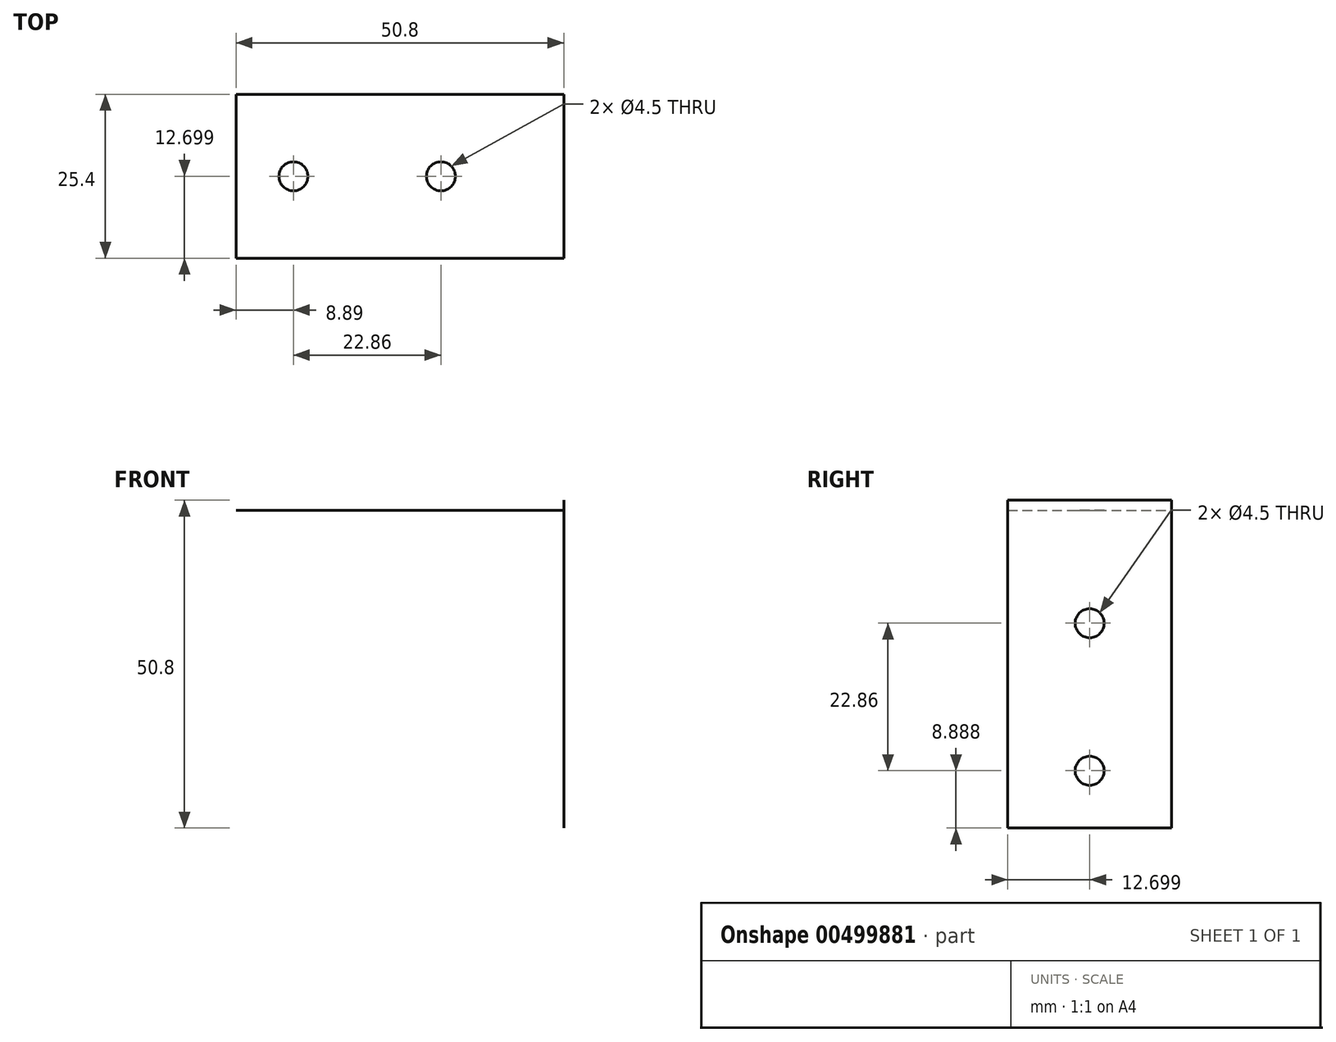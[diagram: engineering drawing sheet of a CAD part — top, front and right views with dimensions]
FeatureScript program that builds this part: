
annotation { "Feature Type Name" : "Feature", "Feature Type Description" : "" }
export const myFeature = defineFeature(function(context is Context, id is Id, definition is map)
    precondition{}
    {
        {
            var Q0;
            Q0=qCreatedBy(makeId("Top.planeOp"),FACE);
            var sketch = newSketch(context, id + "F0", { "sketchPlane" : qUnion([Q0])});
            skPoint(sketch, "E0.middle", {"position": v(0, 0) * mm});
            skLineSegment(sketch, "E1", {"start": v(12.7, 10.32) * mm, "end": v(12.7, -15.08) * mm, "construction": true});
            skLineSegment(sketch, "E2", {"start": v(-10.16, 10.32) * mm, "end": v(-10.16, -15.08) * mm, "construction": true});
            skLineSegment(sketch, "E3.0", {"start": v(31.75, 10.32) * mm, "end": v(-19.05, 10.32) * mm});
            skLineSegment(sketch, "E3.1", {"start": v(31.75, -15.08) * mm, "end": v(31.75, 10.32) * mm});
            skLineSegment(sketch, "E3.2", {"start": v(31.75, -15.08) * mm, "end": v(-19.05, -15.08) * mm});
            skLineSegment(sketch, "E3.3", {"start": v(-19.05, -15.08) * mm, "end": v(-19.05, 10.32) * mm});
            skPoint(sketch, "E4", {"position": v(-10.16, -2.38) * mm});
            skPoint(sketch, "E5", {"position": v(12.7, -2.38) * mm});
            skSolve(sketch);
        }
        {
            var Q0;
            Q0 = qSketchRegion(id + "F0", true);
            extrude(context, id + "F1", {"entities" : qUnion([Q0]), "depth" : 1 / 406.4 * mm});
        }
        {
            var Q0;
            Q0=sQuery(id+"F0.wireOp",VERTEX,"E4");
            var Q1;
            Q1=sQuery(id+"F0.wireOp",VERTEX,"E5");
            var Q2;
            Q2=makeQuery(id+"F1.opExtrude","SWEPT_BODY",BODY,{"disambiguationData":[OSD([sQuery(id+"F0.wireOp",EDGE,"E3.0"),sQuery(id+"F0.wireOp",EDGE,"E3.1"),sQuery(id+"F0.wireOp",EDGE,"E3.2"),sQuery(id+"F0.wireOp",EDGE,"E3.3")])]});
            hole(context, id + "F2", {"style" : HoleStyle.SIMPLE, "endStyle" : HoleEndStyle.THROUGH, "oppositeDirection" : true, "holeDiameter" : 4.5 * mm, "isTappedThrough" : true, "tappedDepth" : 12.7 * mm, "tapClearance" : 3, "locations" : qUnion([Q0, Q1]), "scope" : qUnion([Q2])});
        }
        {
            var Q0;
            Q0=makeQuery(id+"F1.opExtrude","SWEPT_FACE",FACE,{"disambiguationData":[OSD([sQuery(id+"F0.wireOp",EDGE,"E3.1")])]});
            var sketch = newSketch(context, id + "F3", { "sketchPlane" : qUnion([Q0])});
            skLineSegment(sketch, "E6.bottom", {"start": v(10.32, 1.59) * mm, "end": v(-15.08, 1.59) * mm});
            skLineSegment(sketch, "E6.top", {"start": v(10.32, -49.21) * mm, "end": v(-15.08, -49.21) * mm});
            skLineSegment(sketch, "E6.left", {"start": v(10.32, 1.59) * mm, "end": v(10.32, -49.21) * mm});
            skLineSegment(sketch, "E6.right", {"start": v(-15.08, 1.59) * mm, "end": v(-15.08, -49.21) * mm});
            skLineSegment(sketch, "E7", {"start": v(10.32, -17.46) * mm, "end": v(-15.08, -17.46) * mm, "construction": true});
            skLineSegment(sketch, "E8", {"start": v(10.32, -40.32) * mm, "end": v(-15.08, -40.32) * mm, "construction": true});
            skPoint(sketch, "E9", {"position": v(-2.38, -17.46) * mm});
            skPoint(sketch, "E10", {"position": v(-2.38, -40.32) * mm});
            skSolve(sketch);
        }
        {
            var Q0;
            Q0 = qSketchRegion(id + "F3", true);
            extrude(context, id + "F4", {"entities" : qUnion([Q0]), "operationType" : NewBodyOperationType.ADD, "oppositeDirection" : true, "depth" : 1 / 406.4 * mm});
        }
        {
            var Q0;
            Q0=sQuery(id+"F3.wireOp",VERTEX,"E9");
            var Q1;
            Q1=sQuery(id+"F3.wireOp",VERTEX,"E10");
            var Q2;
            Q2=makeQuery(id+"F1.opExtrude","SWEPT_BODY",BODY,{"disambiguationData":[OSD([sQuery(id+"F0.wireOp",EDGE,"E3.0"),sQuery(id+"F0.wireOp",EDGE,"E3.1"),sQuery(id+"F0.wireOp",EDGE,"E3.2"),sQuery(id+"F0.wireOp",EDGE,"E3.3")])]});
            hole(context, id + "F5", {"style" : HoleStyle.SIMPLE, "endStyle" : HoleEndStyle.THROUGH, "holeDiameter" : 4.5 * mm, "isTappedThrough" : true, "tappedDepth" : 12.7 * mm, "tapClearance" : 3, "locations" : qUnion([Q0, Q1]), "scope" : qUnion([Q2])});
        }
    });
